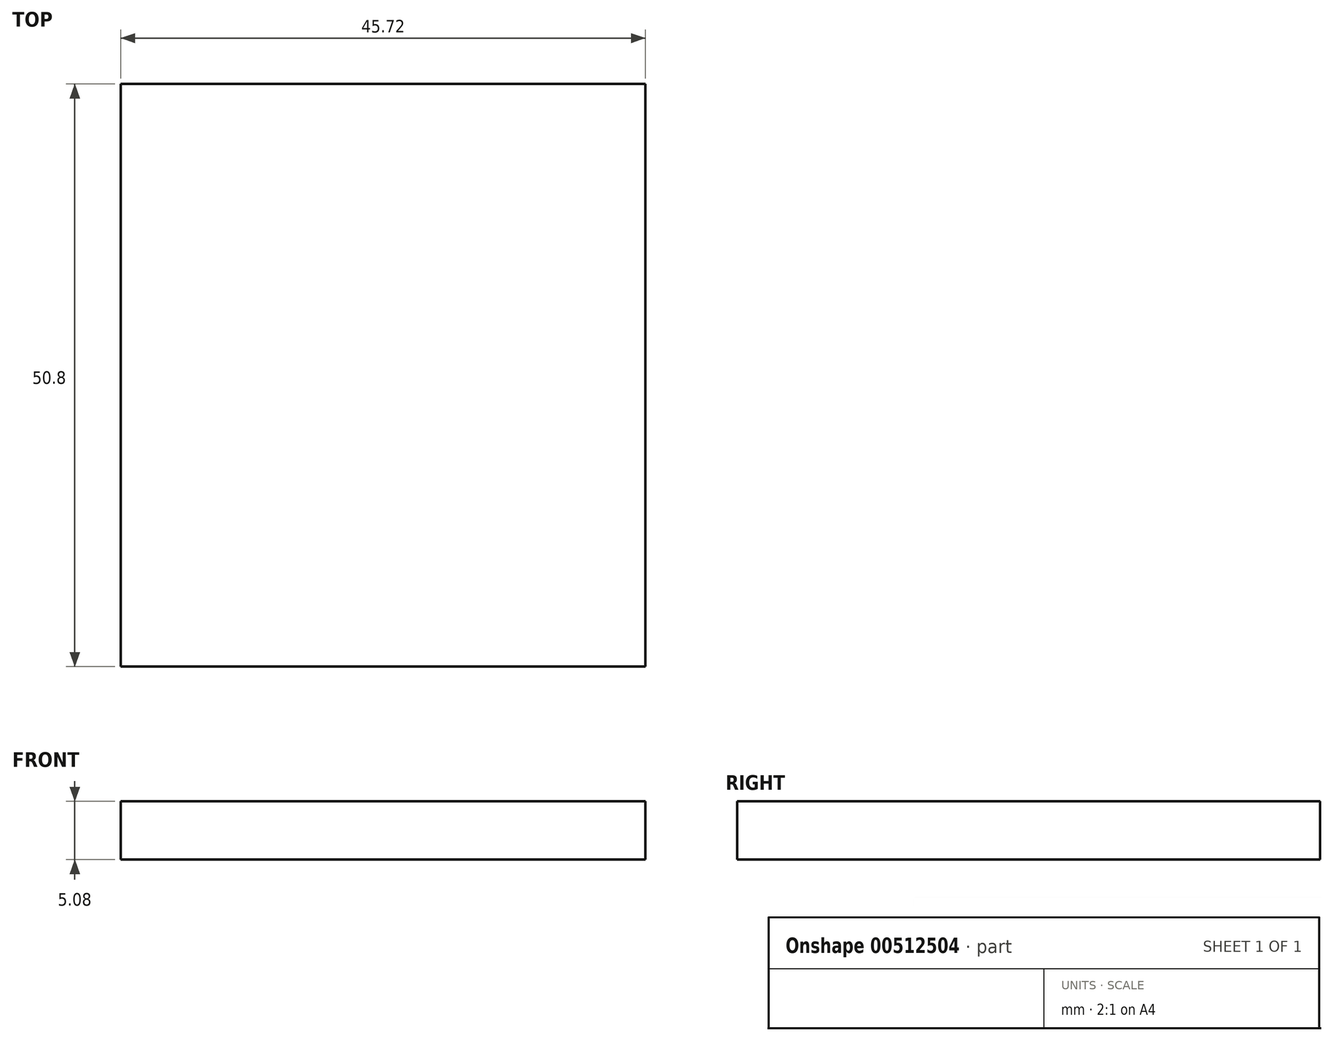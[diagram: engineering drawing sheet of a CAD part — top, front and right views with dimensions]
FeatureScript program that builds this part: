
annotation { "Feature Type Name" : "Feature", "Feature Type Description" : "" }
export const myFeature = defineFeature(function(context is Context, id is Id, definition is map)
    precondition{}
    {
        {
            var Q0;
            Q0=qCreatedBy(makeId("Top.planeOp"),FACE);
            var sketch = newSketch(context, id + "F0", { "sketchPlane" : qUnion([Q0])});
            skLineSegment(sketch, "E0.bottom", {"start": v(-37.06, -28.6) * mm, "end": v(8.66, -28.6) * mm});
            skLineSegment(sketch, "E0.top", {"start": v(-37.06, 22.2) * mm, "end": v(8.66, 22.2) * mm});
            skLineSegment(sketch, "E0.left", {"start": v(-37.06, -28.6) * mm, "end": v(-37.06, 22.2) * mm});
            skLineSegment(sketch, "E0.right", {"start": v(8.66, -28.6) * mm, "end": v(8.66, 22.2) * mm});
            skSolve(sketch);
        }
        {
            var Q0;
            Q0=makeQuery(id+"F0.imprint","IMPRINT",FACE,{"disambiguationData":[TD([[makeQuery(id+"F0.imprint","IMPRINT",EDGE,{"derivedFrom":sQuery(id+"F0.wireOp",EDGE,"E0.bottom")}),1.0]])]});
            extrude(context, id + "F1", {"entities" : qUnion([Q0]), "depth" : 5.08 * mm});
        }
    });
